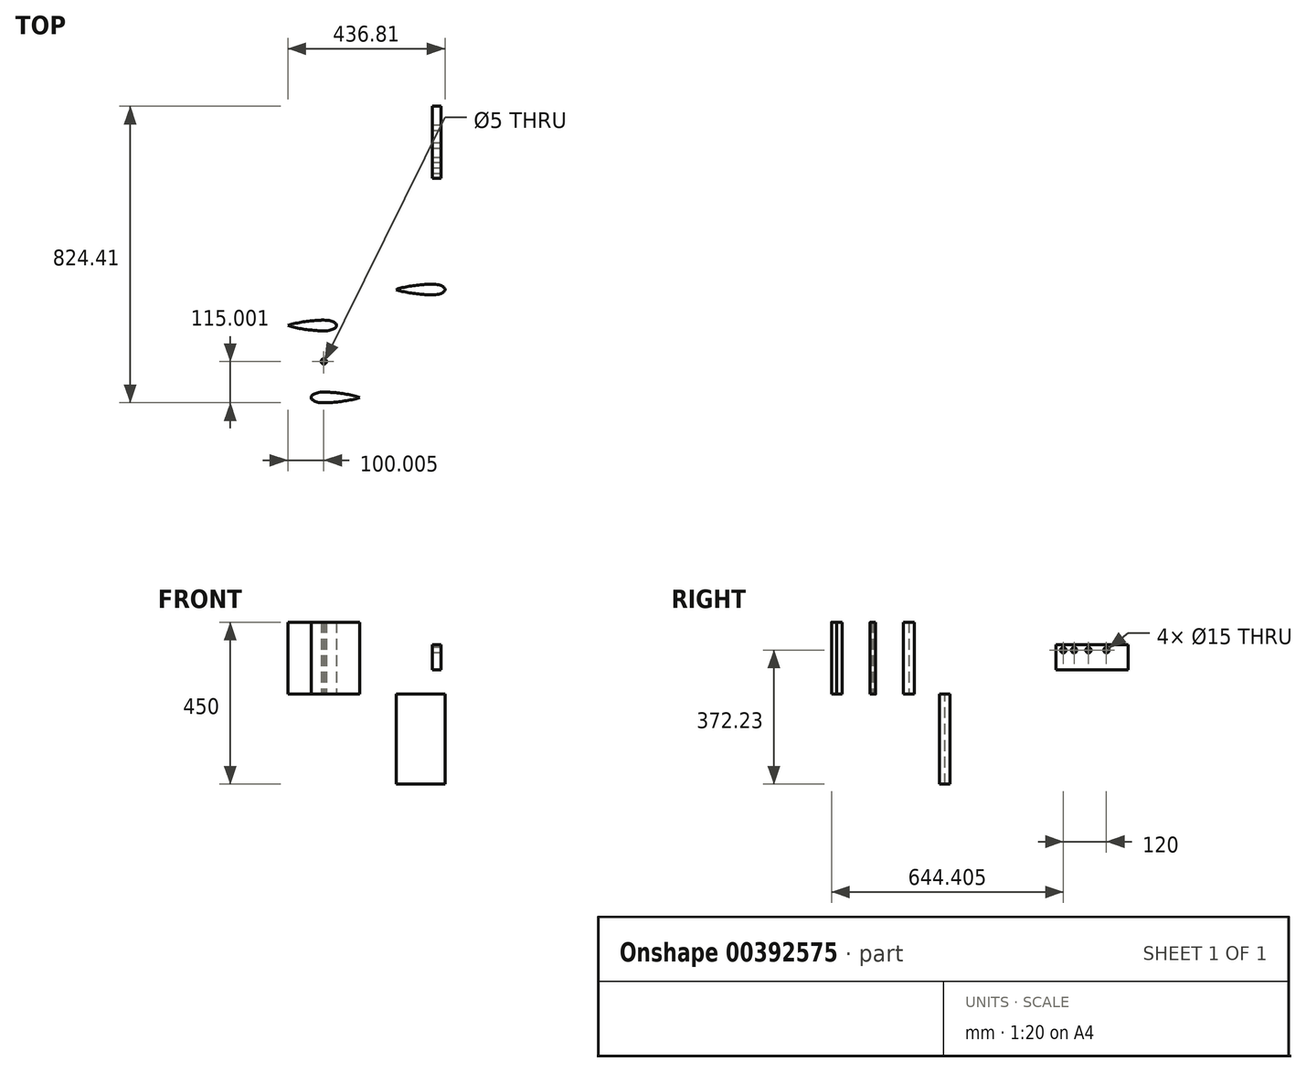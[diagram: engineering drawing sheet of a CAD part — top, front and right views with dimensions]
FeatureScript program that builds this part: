
annotation { "Feature Type Name" : "Feature", "Feature Type Description" : "" }
export const myFeature = defineFeature(function(context is Context, id is Id, definition is map)
    precondition{}
    {
        {
            var Q0;
            Q0=qCreatedBy(makeId("Top.planeOp"),FACE);
            var sketch = newSketch(context, id + "F0", { "sketchPlane" : qUnion([Q0])});
            skPoint(sketch, "E0", {"position": v(-100, 0) * mm});
            skPoint(sketch, "E1", {"position": v(0, 15) * mm});
            skPoint(sketch, "E2", {"position": v(0, -15) * mm});
            skFitSpline(sketch, "E3", {"points": [v(0, 15) * mm, v(-100, 0) * mm], "startDerivative": vector(-48.7, 0) * mm, "endDerivative": vector(-85.27, -32.97) * mm});
            skFitSpline(sketch, "E4.MirrorCS", {"points": [v(0, -15) * mm, v(-100, 0) * mm], "startDerivative": vector(-48.7, 0) * mm, "endDerivative": vector(-85.27, 32.97) * mm});
            skLineSegment(sketch, "E5", {"start": v(0, -15) * mm, "end": v(0, -15) * mm});
            skEllipticalArc(sketch, "E6", {});
            skLineSegment(sketch, "E7", {"start": v(-35.33, 0) * mm, "end": v(-35.33, 0) * mm});
            skLineSegment(sketch, "E8", {"start": v(0, 15) * mm, "end": v(0, 15) * mm});
            skPoint(sketch, "E9", {"position": v(35.33, 0) * mm});
            skPoint(sketch, "E10", {"position": v(-401.48, -99.95) * mm});
            skPoint(sketch, "E11", {"position": v(-301.48, -84.95) * mm});
            skPoint(sketch, "E12", {"position": v(-301.48, -114.95) * mm});
            skFitSpline(sketch, "E13", {"points": [v(-301.48, -84.95) * mm, v(-401.48, -99.95) * mm], "startDerivative": vector(-48.7, 0) * mm, "endDerivative": vector(-85.27, -32.97) * mm});
            skFitSpline(sketch, "E14.MirrorCS", {"points": [v(-301.48, -114.95) * mm, v(-401.48, -99.95) * mm], "startDerivative": vector(-48.7, 0) * mm, "endDerivative": vector(-85.27, 32.97) * mm});
            skLineSegment(sketch, "E15", {"start": v(-301.48, -114.95) * mm, "end": v(-301.48, -114.95) * mm});
            skEllipticalArc(sketch, "E16", {});
            skLineSegment(sketch, "E17", {"start": v(-336.8, -99.95) * mm, "end": v(-336.8, -99.95) * mm});
            skLineSegment(sketch, "E18", {"start": v(-301.48, -84.95) * mm, "end": v(-301.48, -84.95) * mm});
            skPoint(sketch, "E19", {"position": v(-266.14, -99.95) * mm});
            skLineSegment(sketch, "E20", {"start": v(-464.24, -199.95) * mm, "end": v(-112.76, -199.95) * mm, "construction": true});
            skPoint(sketch, "E21.MirrorP", {"position": v(-301.35, -284.95) * mm});
            skPoint(sketch, "E22.MirrorP", {"position": v(-301.35, -314.95) * mm});
            skPoint(sketch, "E23.MirrorP", {"position": v(-536.8, -299.95) * mm});
            skPoint(sketch, "E24.MirrorP", {"position": v(-201.35, -299.95) * mm});
            skEllipticalArc(sketch, "E25.MirrorCS", {});
            skFitSpline(sketch, "E26.MirrorCS", {"points": [v(-301.35, -284.95) * mm, v(-201.35, -299.95) * mm], "startDerivative": vector(48.7, 0) * mm, "endDerivative": vector(85.27, -32.97) * mm});
            skFitSpline(sketch, "E27.MirrorCS", {"points": [v(-301.35, -314.95) * mm, v(-201.35, -299.95) * mm], "startDerivative": vector(48.7, 0) * mm, "endDerivative": vector(85.27, 32.97) * mm});
            skFitSpline(sketch, "E28.MirrorCS", {"points": [v(-301.48, -114.95) * mm, v(-401.48, -99.95) * mm], "startDerivative": vector(-48.7, 0) * mm, "endDerivative": vector(-85.27, 32.97) * mm});
            skLineSegment(sketch, "E29", {"start": v(-301.48, -20.77) * mm, "end": v(-301.48, -408.4) * mm, "construction": true});
            skLineSegment(sketch, "E30", {"start": v(-183.8, -299.95) * mm, "end": v(-578.16, -299.95) * mm, "construction": true});
            skPoint(sketch, "E31", {"position": v(-301.48, -199.95) * mm});
            skCircle(sketch, "E32", {"center": v(-301.48, -199.95) * mm, "radius": 0.01 * mm});
            skCircle(sketch, "E33", {"center": v(-301.48, -199.95) * mm, "radius": 0.03 * mm});
            skCircle(sketch, "E34", {"center": v(-301.48, -199.95) * mm, "radius": 2.5 * mm});
            skCircle(sketch, "E35", {"center": v(-301.48, -199.95) * mm, "radius": 7.5 * mm});
            const initialGuessF0  = {"E6": [0, 0, 0, 1, 0.015, 0.03533193841576576, 3.141592653589793, 6.283185307179586], "E16": [-0.30147545073621745, -0.09994924572644104, 0, 1, 0.015, 0.03533193841576576, 3.141592653589793, 6.283185307179586], "E25.MirrorCS": [-0.301353581188726, -0.2999492457264411, 0, 1, 0.015, 0.03533193841576576, 6.283185307179586, 3.141592653589793], "E16": [-0.30147545073621745, -0.09994924572644104, 0, 1, 0.015, 0.03533193841576576, 3.141592653589793, 6.283185307179586]};
            skSetInitialGuess(sketch, initialGuessF0);
            skSolve(sketch);
        }
        {
            var Q0;
            Q0=makeQuery(id+"F0.imprint","IMPRINT",FACE,{"disambiguationData":[TD([[makeQuery(id+"F0.imprint","IMPRINT",EDGE,{"derivedFrom":sQuery(id+"F0.wireOp",EDGE,"E3")}),1.0]])]});
            extrude(context, id + "F1", {"entities" : qUnion([Q0]), "oppositeDirection" : true, "depth" : 250 * mm});
        }
        {
            var Q0;
            Q0=makeQuery(id+"F0.imprint","IMPRINT",FACE,{"disambiguationData":[TD([[makeQuery(id+"F0.imprint","IMPRINT",EDGE,{"derivedFrom":sQuery(id+"F0.wireOp",EDGE,"E16")}),1.0]])]});
            var Q1;
            Q1=makeQuery(id+"F0.imprint","IMPRINT",FACE,{"disambiguationData":[TD([[makeQuery(id+"F0.imprint","IMPRINT",EDGE,{"derivedFrom":sQuery(id+"F0.wireOp",EDGE,"E25.MirrorCS")}),1.0]])]});
            var Q2;
            Q2=makeQuery(id+"F0.imprint","IMPRINT",FACE,{"disambiguationData":[TD([[makeQuery(id+"F0.imprint","IMPRINT",EDGE,{"derivedFrom":sQuery(id+"F0.wireOp",EDGE,"E34")}),-1.0]])]});
            extrude(context, id + "F2", {"entities" : qUnion([Q0, Q1, Q2]), "depth" : 200 * mm});
        }
        {
            var Q0;
            Q0=qCreatedBy(makeId("Front.planeOp"),FACE);
            cPlane(context, id + "F3", {"entities" : qUnion([Q0]), "cplaneType" : CPlaneType.OFFSET, "offset" : 200 * mm, "width" : 150 * mm, "height" : 150 * mm});
        }
        {
            var Q0;
            Q0=qCreatedBy(id+"F3.planeOp",FACE);
            var sketch = newSketch(context, id + "F4", { "sketchPlane" : qUnion([Q0])});
            skLineSegment(sketch, "E36", {"start": v(-301.63, 0) * mm, "end": v(-301.63, 230.54) * mm, "construction": true});
            skCircle(sketch, "E37", {"center": v(-301.63, 185) * mm, "radius": 6 * mm});
            skCircle(sketch, "E38", {"center": v(-301.63, 15) * mm, "radius": 6 * mm});
            skSolve(sketch);
        }
        {
            var Q0;
            Q0=sQuery(id+"F4.wireOp",EDGE,"E37");
            var Q1;
            Q1=sQuery(id+"F4.wireOp",EDGE,"E38");
            extrude(context, id + "F5", {"bodyType" : ToolBodyType.SURFACE, "surfaceEntities" : qUnion([Q0, Q1]), "endBound" : BoundingType.SYMMETRIC, "depth" : 200 * mm});
        }
        {
            var Q0;
            Q0=qCreatedBy(makeId("Right.planeOp"),FACE);
            var sketch = newSketch(context, id + "F6", { "sketchPlane" : qUnion([Q0])});
            skLineSegment(sketch, "E39.bottom", {"start": v(309.46, 137.23) * mm, "end": v(509.46, 137.23) * mm});
            skLineSegment(sketch, "E39.top", {"start": v(309.46, 67.23) * mm, "end": v(509.46, 67.23) * mm});
            skLineSegment(sketch, "E39.left", {"start": v(309.46, 137.23) * mm, "end": v(309.46, 67.23) * mm});
            skLineSegment(sketch, "E39.right", {"start": v(509.46, 137.23) * mm, "end": v(509.46, 67.23) * mm});
            skCircle(sketch, "E40", {"center": v(329.46, 122.23) * mm, "radius": 7.5 * mm});
            skCircle(sketch, "E41", {"center": v(359.46, 122.23) * mm, "radius": 7.5 * mm});
            skCircle(sketch, "E42", {"center": v(399.46, 122.23) * mm, "radius": 7.5 * mm});
            skCircle(sketch, "E43", {"center": v(449.46, 122.23) * mm, "radius": 7.5 * mm});
            skSolve(sketch);
        }
        {
            var Q0;
            Q0=qSketchRegion(id+"F6",true);
            var Q1;
            Q1=makeQuery(id+"F6.imprint","IMPRINT",FACE,{"disambiguationData":[TD([[makeQuery(id+"F6.imprint","IMPRINT",EDGE,{"derivedFrom":sQuery(id+"F6.wireOp",EDGE,"E39.bottom")}),-1.0]])]});
            extrude(context, id + "F7", {"entities" : qUnion([Q0, Q1]), "depth" : 25 * mm});
        }
    });
